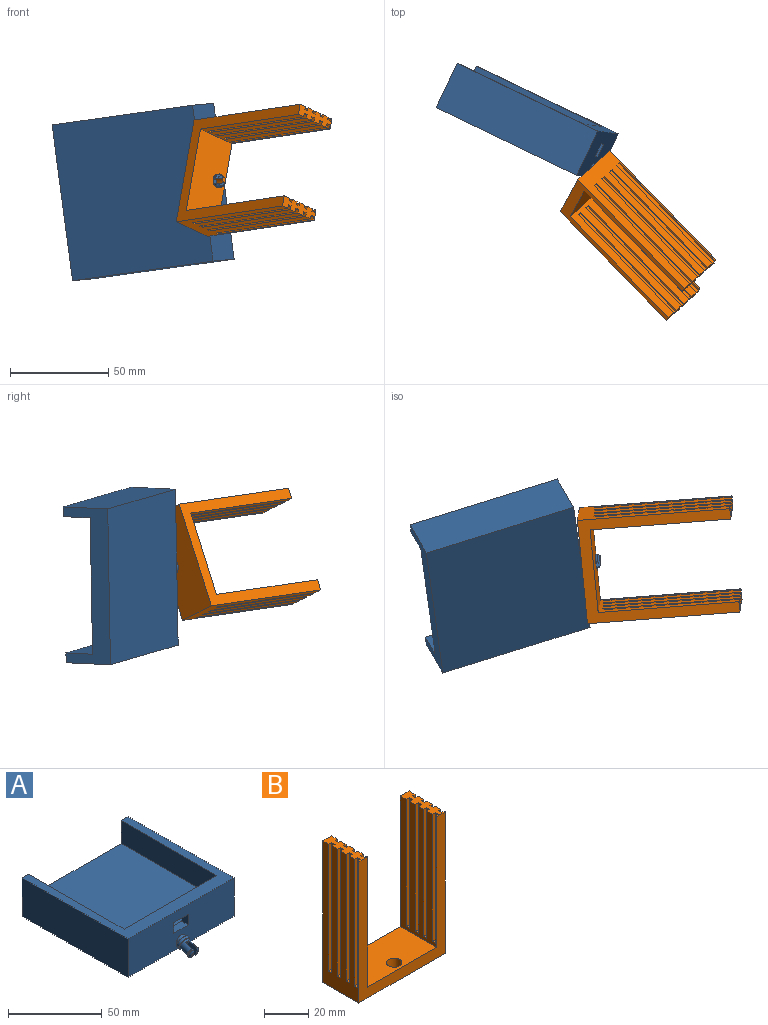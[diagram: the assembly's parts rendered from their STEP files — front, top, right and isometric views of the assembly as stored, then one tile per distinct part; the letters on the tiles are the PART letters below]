
ASSEMBLY  parts=2 mates=1
PART A: 32 faces, bbox 80.3x91.3x27.5 mm
  f0: cylinder r=4mm len=8.1mm, axis (0,-0.94,-0.34), area 40.7mm2, adj f1,f18,f19
  f1: plane 80.26x25.26mm, normal (0,-1,0), area 1883mm2, adj f0,f2,f8,f9,f10,f11,f14,f15
  f2: cylinder r=3.25mm len=6.5mm, axis (0,0.94,0.34), area 19.3mm2, adj f1,f18
  f3: plane 70x10mm, normal (0,1,0), area 623mm2, adj f4,f5,f6,f13,f14,f15,f16,f17
  f4: plane 75x15mm, normal (-1,0,0), area 1110mm2, adj f3,f6,f7,f11,f12,f13
  f5: plane 75x15mm, normal (1,0,0), area 1110mm2, adj f3,f6,f7,f11,f12,f13
  f6: plane 75x70mm, normal (0,0,1), area 5250mm2, adj f3,f4,f5,f7
  f7: plane 80x25mm, normal (0,1,0), area 950mm2, adj f4,f5,f6,f8,f9,f10,f11
  f8: plane 80x25mm, normal (-1,0,0), area 2000mm2, adj f1,f7,f10,f11
  f9: plane 80x25mm, normal (1,0,0), area 2000mm2, adj f1,f7,f10,f11
  f10: plane 80x80mm, normal (0,0,-1), area 6400mm2, adj f1,f7,f8,f9
  f11: plane 80x80mm, normal (0,0,1), area 1360mm2, adj f1,f4,f5,f7,f8,f9,f12
  f12: plane 70x5mm, normal (0,1,0), area 350mm2, adj f4,f5,f11,f13
  f13: plane 70x3mm, normal (0,0,-1), area 210mm2, adj f3,f4,f5,f12
  f14: plane 11x5mm, normal (0,0,-1), area 55mm2, adj f1,f3,f15,f17
  f15: plane 7x5mm, normal (-1,0,0), area 35mm2, adj f1,f3,f14,f16
  f16: plane 11x5mm, normal (0,0,1), area 55mm2, adj f1,f3,f15,f17
  f17: plane 7x5mm, normal (1,0,0), area 35mm2, adj f1,f3,f14,f16
  f18: plane 8x6.1mm, normal (0,0.94,0.34), area 12.7mm2, adj f0,f1,f2
  f19: plane 8x7.52mm, normal (0,-0.94,-0.34), area 17.1mm2, adj f0,f29
  f20: plane 4.07x1.48mm, normal (0,-0.94,-0.34), area 3.8mm2, adj f21,f28
  f21: cone r=2.5mm half-angle=45deg, axis (0,0.94,0.34), area 9.6mm2, adj f20,f22,f28
  f22: cylinder r=3.5mm len=6.49mm, axis (0,-0.94,-0.34), area 8.4mm2, adj f21,f27,f28
  f23: plane 4.07x1.48mm, normal (0,-0.94,-0.34), area 3.8mm2, adj f24,f30
  f24: cone r=2.5mm half-angle=45deg, axis (0,0.94,0.34), area 9.6mm2, adj f23,f25,f30
  f25: cylinder r=3.5mm len=6.49mm, axis (0,-0.94,-0.34), area 8.4mm2, adj f24,f26,f30
  f26: plane 6.14x2.25mm, normal (0,0.94,0.34), area 2mm2, adj f25,f29,f30
  f27: plane 6.14x2.25mm, normal (0,0.94,0.34), area 2mm2, adj f22,f28,f29
  f28: plane 8.43x8.03mm, normal (1,0,0), area 42mm2, adj f20,f21,f22,f27,f29,f31
  f29: cylinder r=3.25mm len=8.26mm, axis (0,0.94,0.34), area 103mm2, adj f19,f26,f27,f28,f30,f31
  f30: plane 8.43x8.03mm, normal (-1,0,0), area 42mm2, adj f23,f24,f25,f26,f29,f31
  f31: plane 6.11x2.5mm, normal (0,-0.94,-0.34), area 15.8mm2, adj f28,f29,f30
PART B: 75 faces, bbox 55x23x78 mm
  f0: plane 78x23mm, normal (1,0,0), area 1234mm2, adj f1,f5,f7,f8,f47,f49,f50,f51
  f1: plane 23x5.5mm, normal (0,0,1), area 98.5mm2, adj f0,f5,f7,f10,f43,f44,f45,f47
  f2: plane 72x23mm, normal (1,0,0), area 1096mm2, adj f3,f4,f5,f7,f15,f17,f18,f19
  f3: plane 23x5.5mm, normal (0,0,1), area 98.5mm2, adj f2,f5,f6,f7,f11,f12,f13,f15
  f4: plane 44x23mm, normal (0,0,1), area 973.5mm2, adj f2,f5,f7,f9,f10
  f5: plane 78x55mm, normal (0,1,0), area 1122mm2, adj f0,f1,f2,f3,f4,f6,f8,f10
  f6: plane 78x23mm, normal (-1,0,0), area 1234mm2, adj f3,f5,f7,f8,f11,f12,f14,f27
  f7: plane 78x55mm, normal (0,-1,0), area 1122mm2, adj f0,f1,f2,f3,f4,f6,f8,f10
  f8: plane 55x23mm, normal (0,0,-1), area 1226.5mm2, adj f0,f5,f6,f7,f9
  f9: cylinder r=3.5mm len=7mm, axis (0,0,1), area 131.9mm2, adj f4,f8
  f10: plane 72x23mm, normal (-1,0,0), area 1096mm2, adj f1,f4,f5,f7,f43,f44,f46,f59
  f11: plane 70x2mm, normal (0,-1,0), area 140mm2, adj f3,f6,f13,f14
  f12: plane 70x2mm, normal (0,1,0), area 140mm2, adj f3,f6,f13,f14
  f13: plane 70x2mm, normal (-1,0,0), area 140mm2, adj f3,f11,f12,f14
  f14: plane 2x2mm, normal (0,0,1), area 4mm2, adj f6,f11,f12,f13
  f15: plane 70x1.5mm, normal (0,-1,0), area 105mm2, adj f2,f3,f16,f18
  f16: plane 70x2mm, normal (1,0,0), area 140mm2, adj f3,f15,f17,f18
  f17: plane 70x1.5mm, normal (0,1,0), area 105mm2, adj f2,f3,f16,f18
  f18: plane 2x1.5mm, normal (0,0,1), area 3mm2, adj f2,f15,f16,f17
  f19: plane 70x1.5mm, normal (0,-1,0), area 105mm2, adj f2,f3,f20,f22
  f20: plane 70x2mm, normal (1,0,0), area 140mm2, adj f3,f19,f21,f22
  f21: plane 70x1.5mm, normal (0,1,0), area 105mm2, adj f2,f3,f20,f22
  f22: plane 2x1.5mm, normal (0,0,1), area 3mm2, adj f2,f19,f20,f21
  f23: plane 70x1.5mm, normal (0,-1,0), area 105mm2, adj f2,f3,f24,f26
  f24: plane 70x2mm, normal (1,0,0), area 140mm2, adj f3,f23,f25,f26
  f25: plane 70x1.5mm, normal (0,1,0), area 105mm2, adj f2,f3,f24,f26
  f26: plane 2x1.5mm, normal (0,0,1), area 3mm2, adj f2,f23,f24,f25
  f27: plane 70x2mm, normal (0,1,0), area 140mm2, adj f3,f6,f28,f30
  f28: plane 70x2mm, normal (-1,0,0), area 140mm2, adj f3,f27,f29,f30
  f29: plane 70x2mm, normal (0,-1,0), area 140mm2, adj f3,f6,f28,f30
  f30: plane 2x2mm, normal (0,0,1), area 4mm2, adj f6,f27,f28,f29
  f31: plane 70x2mm, normal (0,1,0), area 140mm2, adj f3,f6,f32,f34
  f32: plane 70x2mm, normal (-1,0,0), area 140mm2, adj f3,f31,f33,f34
  f33: plane 70x2mm, normal (0,-1,0), area 140mm2, adj f3,f6,f32,f34
  f34: plane 2x2mm, normal (0,0,1), area 4mm2, adj f6,f31,f32,f33
  f35: plane 70x2mm, normal (0,1,0), area 140mm2, adj f3,f6,f36,f38
  f36: plane 70x2mm, normal (-1,0,0), area 140mm2, adj f3,f35,f37,f38
  f37: plane 70x2mm, normal (0,-1,0), area 140mm2, adj f3,f6,f36,f38
  f38: plane 2x2mm, normal (0,0,1), area 4mm2, adj f6,f35,f36,f37
  f39: plane 70x1.5mm, normal (0,-1,0), area 105mm2, adj f2,f3,f40,f42
  f40: plane 70x2mm, normal (1,0,0), area 140mm2, adj f3,f39,f41,f42
  f41: plane 70x1.5mm, normal (0,1,0), area 105mm2, adj f2,f3,f40,f42
  f42: plane 2x1.5mm, normal (0,0,1), area 3mm2, adj f2,f39,f40,f41
  f43: plane 70x2mm, normal (0,-1,0), area 140mm2, adj f1,f10,f45,f46
  f44: plane 70x2mm, normal (0,1,0), area 140mm2, adj f1,f10,f45,f46
  f45: plane 70x2mm, normal (-1,0,0), area 140mm2, adj f1,f43,f44,f46
  f46: plane 2x2mm, normal (0,0,1), area 4mm2, adj f10,f43,f44,f45
  f47: plane 70x1.5mm, normal (0,-1,0), area 105mm2, adj f0,f1,f48,f50
  f48: plane 70x2mm, normal (1,0,0), area 140mm2, adj f1,f47,f49,f50
  f49: plane 70x1.5mm, normal (0,1,0), area 105mm2, adj f0,f1,f48,f50
  f50: plane 2x1.5mm, normal (0,0,1), area 3mm2, adj f0,f47,f48,f49
  f51: plane 70x1.5mm, normal (0,-1,0), area 105mm2, adj f0,f1,f52,f54
  f52: plane 70x2mm, normal (1,0,0), area 140mm2, adj f1,f51,f53,f54
  f53: plane 70x1.5mm, normal (0,1,0), area 105mm2, adj f0,f1,f52,f54
  f54: plane 2x1.5mm, normal (0,0,1), area 3mm2, adj f0,f51,f52,f53
  f55: plane 70x1.5mm, normal (0,-1,0), area 105mm2, adj f0,f1,f56,f58
  f56: plane 70x2mm, normal (1,0,0), area 140mm2, adj f1,f55,f57,f58
  f57: plane 70x1.5mm, normal (0,1,0), area 105mm2, adj f0,f1,f56,f58
  f58: plane 2x1.5mm, normal (0,0,1), area 3mm2, adj f0,f55,f56,f57
  f59: plane 70x2mm, normal (0,1,0), area 140mm2, adj f1,f10,f60,f62
  f60: plane 70x2mm, normal (-1,0,0), area 140mm2, adj f1,f59,f61,f62
  f61: plane 70x2mm, normal (0,-1,0), area 140mm2, adj f1,f10,f60,f62
  f62: plane 2x2mm, normal (0,0,1), area 4mm2, adj f10,f59,f60,f61
  f63: plane 70x2mm, normal (0,1,0), area 140mm2, adj f1,f10,f64,f66
  f64: plane 70x2mm, normal (-1,0,0), area 140mm2, adj f1,f63,f65,f66
  f65: plane 70x2mm, normal (0,-1,0), area 140mm2, adj f1,f10,f64,f66
  f66: plane 2x2mm, normal (0,0,1), area 4mm2, adj f10,f63,f64,f65
  f67: plane 70x2mm, normal (0,1,0), area 140mm2, adj f1,f10,f68,f70
  f68: plane 70x2mm, normal (-1,0,0), area 140mm2, adj f1,f67,f69,f70
  f69: plane 70x2mm, normal (0,-1,0), area 140mm2, adj f1,f10,f68,f70
  f70: plane 2x2mm, normal (0,0,1), area 4mm2, adj f10,f67,f68,f69
  f71: plane 70x1.5mm, normal (0,-1,0), area 105mm2, adj f0,f1,f72,f74
  f72: plane 70x2mm, normal (1,0,0), area 140mm2, adj f1,f71,f73,f74
  f73: plane 70x1.5mm, normal (0,1,0), area 105mm2, adj f0,f1,f72,f74
  f74: plane 2x1.5mm, normal (0,0,1), area 3mm2, adj f0,f71,f72,f73
PLACE A rot(axis=(-0.52,0.72,0.45),101.5deg) t=(-85.13,-144.1,26.48)mm
PLACE B rot(axis=(0.71,-0.17,0.68),133.2deg) t=(-52.47,-167.97,33.81)mm
MATE cylindrical A.f0 <-> B.f9  axis (-0.69,0.71,-0.1) through (-49.07,-162.64,31.54)mm
